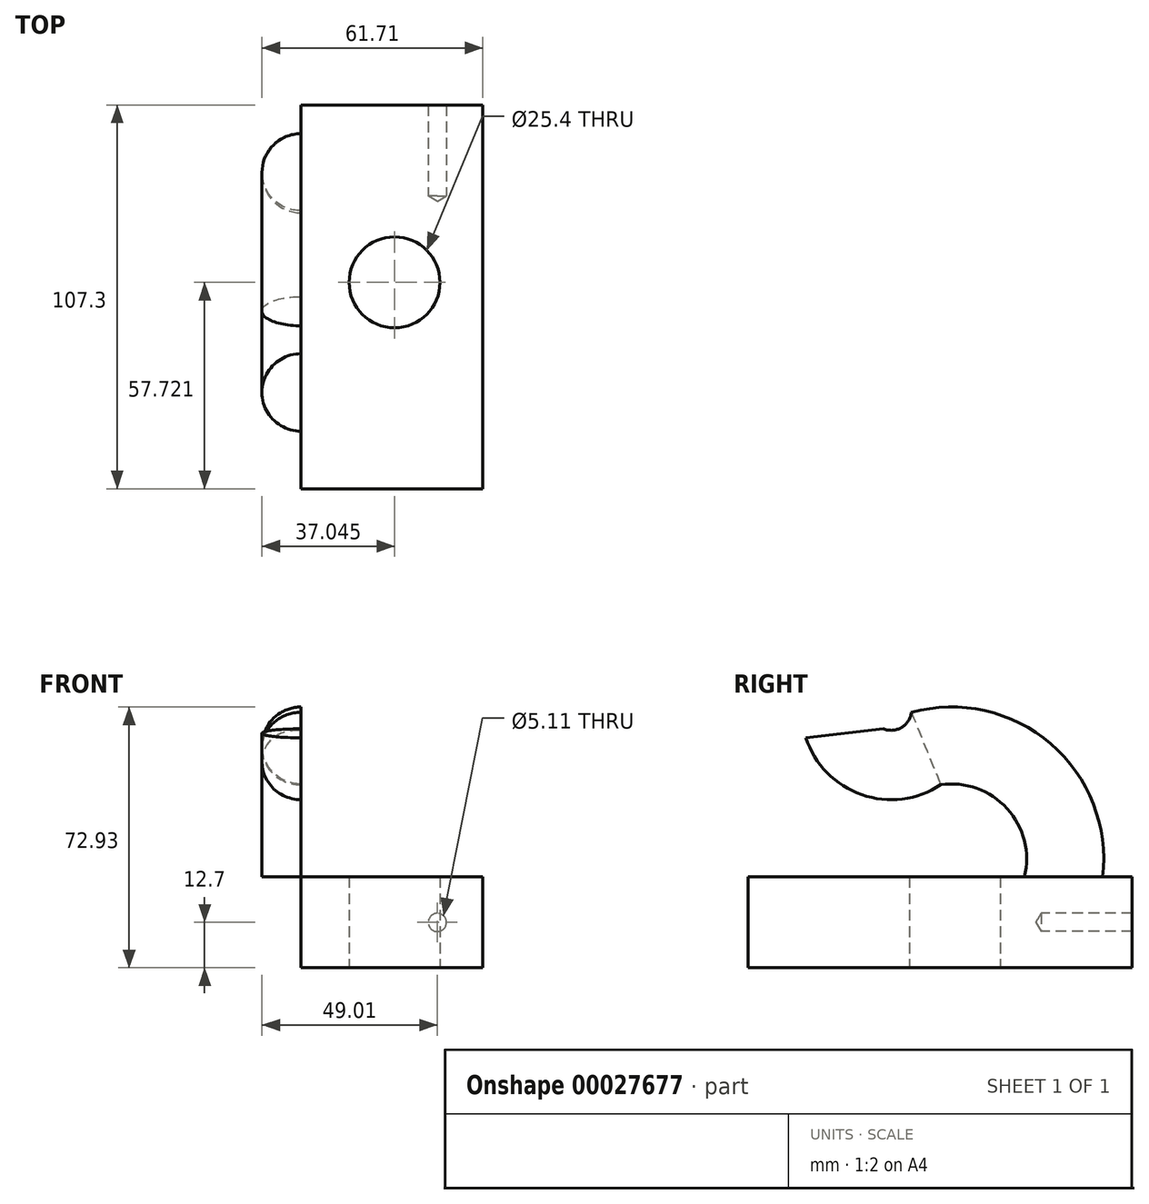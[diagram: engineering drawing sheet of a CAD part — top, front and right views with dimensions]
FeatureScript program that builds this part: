
annotation { "Feature Type Name" : "Feature", "Feature Type Description" : "" }
export const myFeature = defineFeature(function(context is Context, id is Id, definition is map)
    precondition{}
    {
        {
            var Q0;
            Q0=qCreatedBy(makeId("Top.planeOp"),FACE);
            var sketch = newSketch(context, id + "F0", { "sketchPlane" : qUnion([Q0])});
            skLineSegment(sketch, "E0.bottom", {"start": v(0, 0) * mm, "end": v(50.8, 0) * mm});
            skLineSegment(sketch, "E0.top", {"start": v(0, 107.3) * mm, "end": v(50.8, 107.3) * mm});
            skLineSegment(sketch, "E0.left", {"start": v(0, 0) * mm, "end": v(0, 107.3) * mm});
            skLineSegment(sketch, "E0.right", {"start": v(50.8, 0) * mm, "end": v(50.8, 107.3) * mm});
            skCircle(sketch, "E1", {"center": v(26.14, 57.72) * mm, "radius": 12.7 * mm});
            skSolve(sketch);
        }
        {
            var Q0;
            Q0 = qSketchRegion(id + "F0", true);
            extrude(context, id + "F1", {"entities" : qUnion([Q0]), "depth" : 25.4 * mm});
        }
        {
            var Q0;
            Q0=makeQuery(id+"F1.opExtrude","SWEPT_FACE",FACE,{"disambiguationData":[OSD([sQuery(id+"F0.wireOp",EDGE,"E0.top")])]});
            var sketch = newSketch(context, id + "F2", { "sketchPlane" : qUnion([Q0])});
            skPoint(sketch, "E2", {"position": v(-38.1, 12.7) * mm});
            skSolve(sketch);
        }
        {
            var Q0;
            Q0=sQuery(id+"F2.wireOp",VERTEX,"E2");
            var Q1;
            Q1=makeQuery(id+"F1.opExtrude","SWEPT_BODY",BODY,{"disambiguationData":[OSD([sQuery(id+"F0.wireOp",EDGE,"E0.bottom"),sQuery(id+"F0.wireOp",EDGE,"E0.top"),sQuery(id+"F0.wireOp",EDGE,"E0.left"),sQuery(id+"F0.wireOp",EDGE,"E0.right"),sQuery(id+"F0.wireOp",EDGE,"E1")])]});
            hole(context, id + "F3", {"style" : HoleStyle.SIMPLE, "endStyle" : HoleEndStyle.BLIND, "standardTappedOrClearance" : lookupTablePath({ "standard" : "ANSI", "fit" : "Normal (ASME)", "engagement" : "75%", "pitch" : "20 tpi", "size" : "1/4", "type" : "Tapped" }), "standardBlindInLast" : lookupTablePath({ "fit" : "Free", "standard" : "ANSI", "engagement" : "75%", "pitch" : "20 tpi", "size" : "1/4", "type" : "Tapped" }), "holeDiameter" : 5.1 * mm, "holeDepth" : 25.4 * mm, "locations" : qUnion([Q0]), "scope" : qUnion([Q1]), "majorDiameter" : 6.35 * mm});
        }
        {
            var Q0;
            Q0=qCreatedBy(makeId("Right.planeOp"),FACE);
            var sketch = newSketch(context, id + "F4", { "sketchPlane" : qUnion([Q0])});
            skLineSegment(sketch, "E3", {"start": v(87.97, 30.4) * mm, "end": v(87.97, 25.54) * mm});
            skArc(sketch, "E4", {"start": v(87.97, 30.4) * mm, "mid": v(74.22, 56.25) * mm, "end": v(45.1, 59.3) * mm});
            skArc(sketch, "E5", {"start": v(45.1, 59.3) * mm, "mid": v(32.89, 60.23) * mm, "end": v(26.23, 70.5) * mm});
            skSolve(sketch);
        }
        {
            var Q0;
            Q0=makeQuery(id+"F1.opExtrude","CAP_FACE",FACE,{"disambiguationData":[OSD([sQuery(id+"F0.wireOp",EDGE,"E0.bottom"),sQuery(id+"F0.wireOp",EDGE,"E0.top"),sQuery(id+"F0.wireOp",EDGE,"E0.left"),sQuery(id+"F0.wireOp",EDGE,"E0.right"),sQuery(id+"F0.wireOp",EDGE,"E1")])],"isStart":false});
            var sketch = newSketch(context, id + "F5", { "sketchPlane" : qUnion([Q0])});
            skCircle(sketch, "E6", {"center": v(0, 88.11) * mm, "radius": 10.91 * mm});
            skSolve(sketch);
        }
        {
            var Q0;
            {var subQ0=sQuery(id+"F5.wireOp",EDGE,"E6");var subQ1=makeQuery(id+"F1.opExtrude","CAP_EDGE",EDGE,{"disambiguationData":[OSD([sQuery(id+"F0.wireOp",EDGE,"E0.left")])],"isStart":false});var subQ2=makeQuery(id+"F5.imprint","INTERSECT",VERTEX,{"disambiguationData":[OD(0.0)],"derivedFrom":[subQ1,subQ0]});Q0=makeQuery(id+"F5.imprint","IMPRINT",FACE,{"disambiguationData":[TD([[makeQuery(id+"F5.imprint","IMPRINT",EDGE,{"disambiguationData":[TD([[subQ2,1.0]])],"derivedFrom":subQ0}),1.0]])]});}
            var Q1;
            Q1=sQuery(id+"F4.wireOp",EDGE,"E4");
            var Q2;
            Q2=sQuery(id+"F4.wireOp",EDGE,"E5");
            sweep(context, id + "F6", {"profiles" : qUnion([Q0]), "path" : qUnion([Q1, Q2])});
        }
    });
